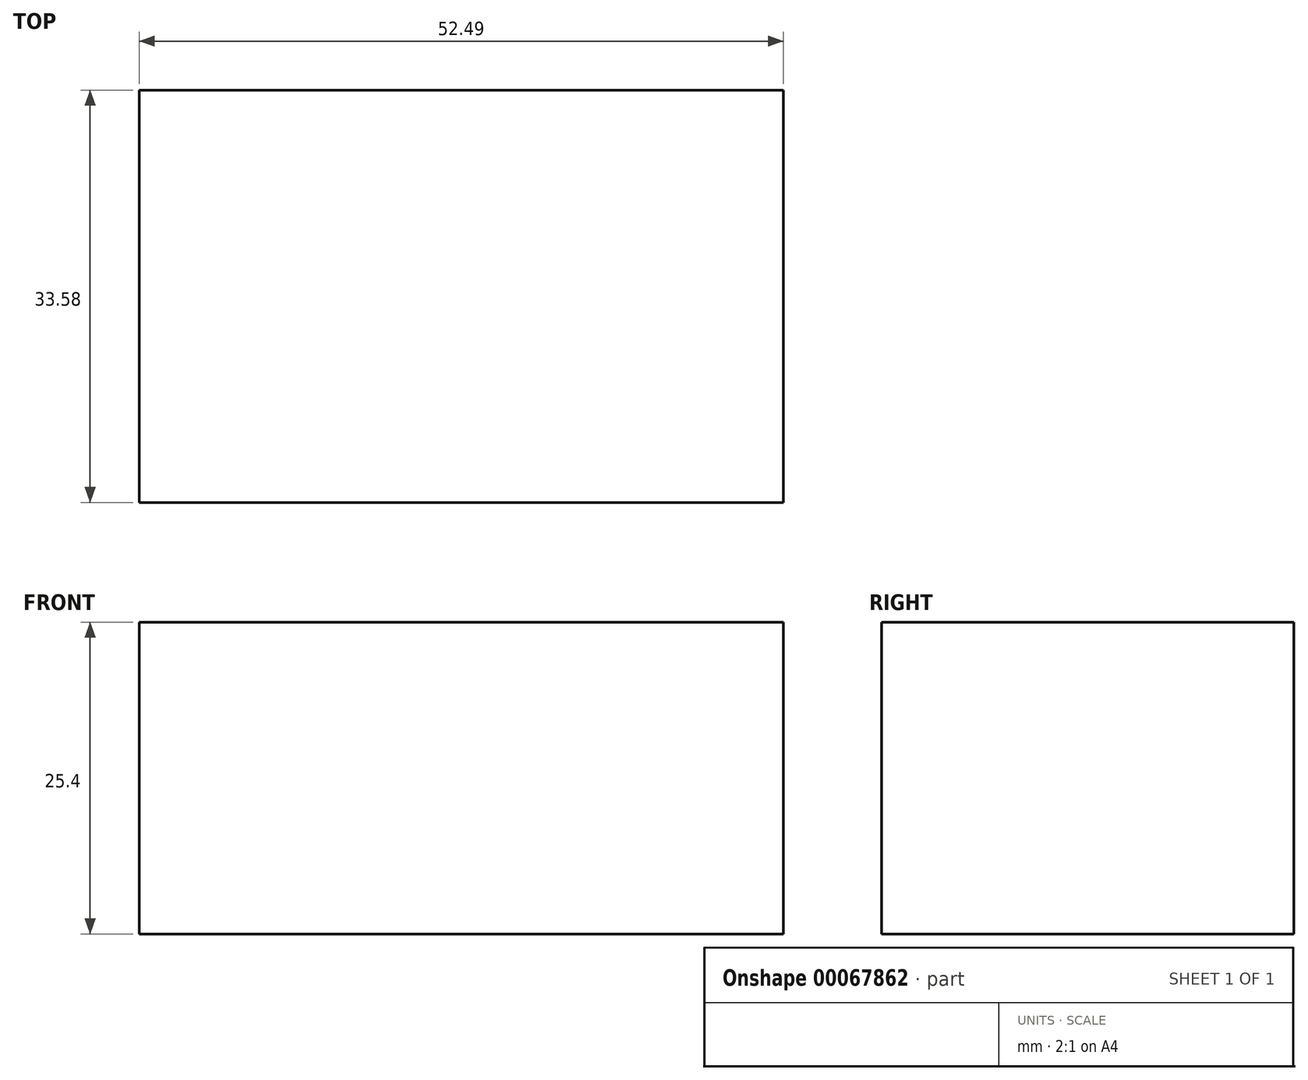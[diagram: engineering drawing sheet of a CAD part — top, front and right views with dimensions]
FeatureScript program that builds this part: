
annotation { "Feature Type Name" : "Feature", "Feature Type Description" : "" }
export const myFeature = defineFeature(function(context is Context, id is Id, definition is map)
    precondition{}
    {
        {
            var Q0;
            Q0=qCreatedBy(makeId("Top.planeOp"),FACE);
            var sketch = newSketch(context, id + "F0", { "sketchPlane" : qUnion([Q0])});
            skLineSegment(sketch, "E0", {"start": v(0, 40.22) * mm, "end": v(0, -52.07) * mm, "construction": true});
            skLineSegment(sketch, "E1.bottom", {"start": v(-24.27, 9.45) * mm, "end": v(28.22, 9.45) * mm});
            skLineSegment(sketch, "E1.top", {"start": v(-24.27, -24.13) * mm, "end": v(28.22, -24.13) * mm});
            skLineSegment(sketch, "E1.left", {"start": v(-24.27, 9.45) * mm, "end": v(-24.27, -24.13) * mm});
            skLineSegment(sketch, "E1.right", {"start": v(28.22, 9.45) * mm, "end": v(28.22, -24.13) * mm});
            skSolve(sketch);
        }
        {
            var Q0;
            Q0 = qSketchRegion(id + "F0", true);
            extrude(context, id + "F1", {"entities" : qUnion([Q0]), "depth" : 25.4 * mm});
        }
    });
